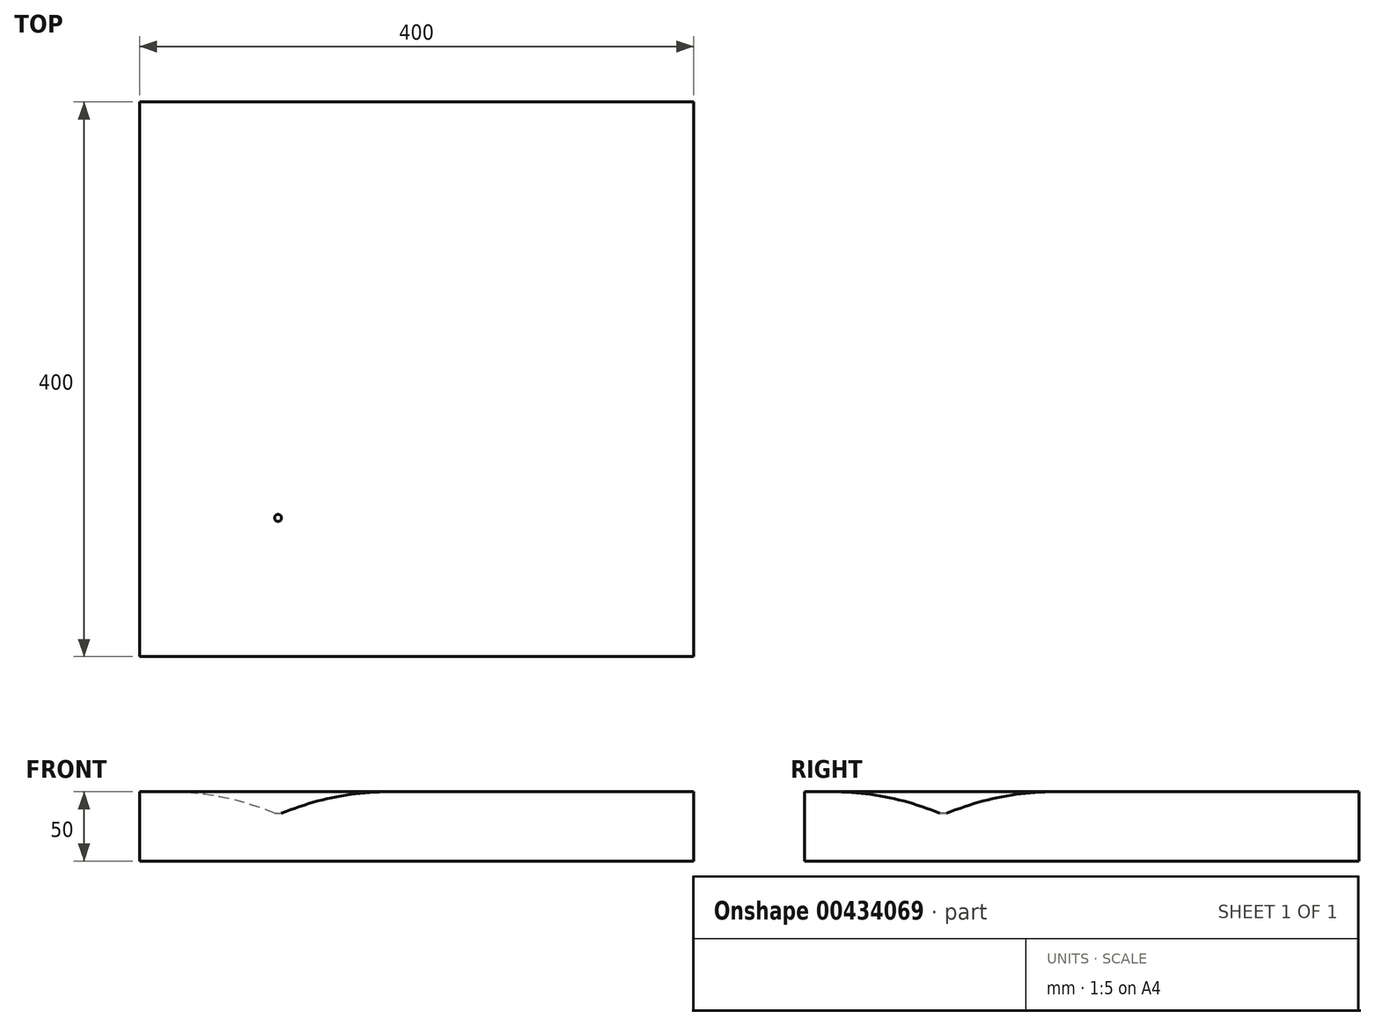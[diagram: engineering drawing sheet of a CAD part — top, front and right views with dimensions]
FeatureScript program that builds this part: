
annotation { "Feature Type Name" : "Feature", "Feature Type Description" : "" }
export const myFeature = defineFeature(function(context is Context, id is Id, definition is map)
    precondition{}
    {
        {
            var Q0;
            Q0=qCreatedBy(makeId("Front.planeOp"),FACE);
            var sketch = newSketch(context, id + "F0", { "sketchPlane" : qUnion([Q0])});
            skLineSegment(sketch, "E0.bottom", {"start": v(200, -25) * mm, "end": v(-200, -25) * mm});
            skLineSegment(sketch, "E0.top", {"start": v(200, 25) * mm, "end": v(-200, 25) * mm});
            skLineSegment(sketch, "E0.left", {"start": v(200, -25) * mm, "end": v(200, 25) * mm});
            skLineSegment(sketch, "E0.right", {"start": v(-200, -25) * mm, "end": v(-200, 25) * mm});
            skPoint(sketch, "E0.middle", {"position": v(0, 0) * mm});
            skSolve(sketch);
        }
        {
            var Q0;
            Q0=makeQuery(id+"F0.imprint","IMPRINT",FACE,{"disambiguationData":[TD([[makeQuery(id+"F0.imprint","IMPRINT",EDGE,{"derivedFrom":sQuery(id+"F0.wireOp",EDGE,"E0.bottom")}),-1.0]])]});
            extrude(context, id + "F1", {"entities" : qUnion([Q0]), "endBound" : BoundingType.SYMMETRIC, "depth" : 400 * mm});
        }
        {
            var Q0;
            Q0=makeQuery(id+"F1.opExtrude","CAP_FACE",FACE,{"disambiguationData":[OSD([sQuery(id+"F0.wireOp",EDGE,"E0.bottom"),sQuery(id+"F0.wireOp",EDGE,"E0.top"),sQuery(id+"F0.wireOp",EDGE,"E0.left"),sQuery(id+"F0.wireOp",EDGE,"E0.right")])],"isStart":false});
            cPlane(context, id + "F2", {"entities" : qUnion([Q0]), "cplaneType" : CPlaneType.OFFSET, "offset" : 100 * mm, "oppositeDirection" : true, "width" : 150 * mm, "height" : 150 * mm});
        }
        {
            var Q0;
            Q0=qCreatedBy(id+"F2.planeOp",FACE);
            var sketch = newSketch(context, id + "F3", { "sketchPlane" : qUnion([Q0])});
            skLineSegment(sketch, "E1", {"start": v(-100, 55.26) * mm, "end": v(-100, -62.5) * mm, "construction": true});
            skLineSegment(sketch, "E2", {"start": v(100, 58.08) * mm, "end": v(100, -55.26) * mm, "construction": true});
            skLineSegment(sketch, "E3", {"start": v(-207.11, -25) * mm, "end": v(-31.46, -25) * mm, "construction": true});
            skLineSegment(sketch, "E4", {"start": v(-208.79, 25) * mm, "end": v(208.15, 25) * mm, "construction": true});
            skLineSegment(sketch, "E5", {"start": v(-100, 25) * mm, "end": v(-180, 25) * mm});
            skArc(sketch, "E6", {"start": v(-102.5, 9.38) * mm, "mid": v(-140.47, 21.06) * mm, "end": v(-180, 25) * mm});
            skLineSegment(sketch, "E7", {"start": v(-102.5, 9.38) * mm, "end": v(-100, 9.38) * mm});
            skLineSegment(sketch, "E8", {"start": v(-100, 9.38) * mm, "end": v(-100, 25) * mm});
            skLineSegment(sketch, "E9", {"start": v(-7.11, -25) * mm, "end": v(168.54, -25) * mm, "construction": true});
            skLineSegment(sketch, "E10", {"start": v(-8.79, 25) * mm, "end": v(149.9, 25) * mm, "construction": true});
            skLineSegment(sketch, "E11", {"start": v(100, 25) * mm, "end": v(20, 25) * mm});
            skArc(sketch, "E12", {"start": v(97.5, 9.38) * mm, "mid": v(59.53, 21.06) * mm, "end": v(20, 25) * mm});
            skLineSegment(sketch, "E13", {"start": v(97.5, 9.38) * mm, "end": v(100, 9.38) * mm});
            skLineSegment(sketch, "E14", {"start": v(100, 9.38) * mm, "end": v(100, 25) * mm});
            skSolve(sketch);
        }
        {
            var Q0;
            Q0=makeQuery(id+"F3.imprint","IMPRINT",FACE,{"disambiguationData":[TD([[makeQuery(id+"F3.imprint","IMPRINT",EDGE,{"derivedFrom":sQuery(id+"F3.wireOp",EDGE,"E5")}),1.0]])]});
            var Q1;
            Q1=sQuery(id+"F3.wireOp",EDGE,"E1");
            revolve(context, id + "F4", {"operationType" : NewBodyOperationType.REMOVE, "entities" : qUnion([Q0]), "axis" : qUnion([Q1]), "revolveType" : RevolveType.FULL, "oppositeDirection" : true});
        }
    });
